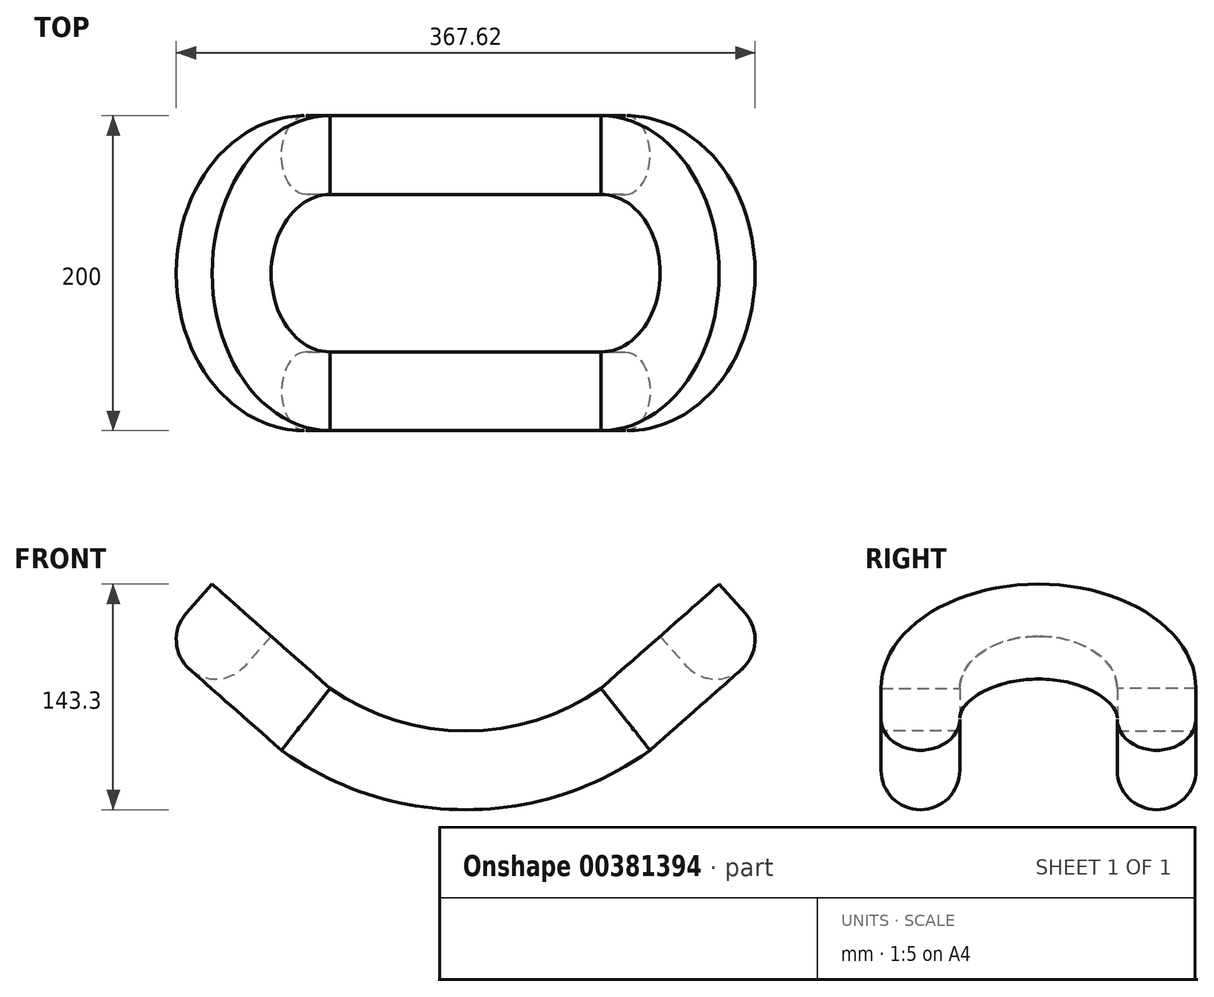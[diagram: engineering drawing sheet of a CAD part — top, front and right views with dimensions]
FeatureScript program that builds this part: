
annotation { "Feature Type Name" : "Feature", "Feature Type Description" : "" }
export const myFeature = defineFeature(function(context is Context, id is Id, definition is map)
    precondition{}
    {
        {
            var Q0;
            Q0=qCreatedBy(makeId("Front.planeOp"),FACE);
            var sketch = newSketch(context, id + "F0", { "sketchPlane" : qUnion([Q0])});
            skArc(sketch, "E0", {"start": v(0, 0) * mm, "mid": v(45.1, 6.94) * mm, "end": v(86.04, 27.13) * mm});
            skLineSegment(sketch, "E1", {"start": v(0, 150) * mm, "end": v(86.04, 27.13) * mm, "construction": true});
            skLineSegment(sketch, "E2", {"start": v(86.04, 27.13) * mm, "end": v(161.01, 93.3) * mm});
            skSolve(sketch);
        }
        {
            var Q0;
            Q0=sQuery(id+"F0.wireOp",EDGE,"E0");
            var Q1;
            Q1=sQuery(id+"F0.wireOp",EDGE,"E2");
            extrude(context, id + "F1", {"bodyType" : ExtendedToolBodyType.SURFACE, "surfaceEntities" : qUnion([Q0, Q1]), "depth" : 100 * mm});
        }
        {
            var Q0;
            Q0=makeQuery(id+"F1.opExtrude","SWEPT_FACE",FACE,{"disambiguationData":[OSD([sQuery(id+"F0.wireOp",EDGE,"E2")])]});
            var sketch = newSketch(context, id + "F2", { "sketchPlane" : qUnion([Q0])});
            skArc(sketch, "E3", {"start": v(82.46, 100) * mm, "mid": v(153.17, 70.71) * mm, "end": v(182.46, 0) * mm});
            skSolve(sketch);
        }
        {
            var Q0;
            Q0=qCreatedBy(makeId("Right.planeOp"),FACE);
            var sketch = newSketch(context, id + "F3", { "sketchPlane" : qUnion([Q0])});
            skLineSegment(sketch, "E4.bottom", {"start": v(-100, 0) * mm, "end": v(-50, 0) * mm});
            skLineSegment(sketch, "E4.left", {"start": v(-100, 0) * mm, "end": v(-100, -25) * mm});
            skLineSegment(sketch, "E4.right", {"start": v(-50, 0) * mm, "end": v(-50, -25) * mm});
            skArc(sketch, "E5", {"start": v(-100, -25) * mm, "mid": v(-75, -50) * mm, "end": v(-50, -25) * mm});
            skSolve(sketch);
        }
        {
            var Q0;
            Q0=makeQuery(id+"F3.imprint","IMPRINT",FACE,{"disambiguationData":[TD([[makeQuery(id+"F3.imprint","IMPRINT",EDGE,{"derivedFrom":sQuery(id+"F3.wireOp",EDGE,"E4.bottom")}),-1.0]])]});
            var Q1;
            Q1=makeQuery(id+"F1.opExtrude","CAP_EDGE",EDGE,{"disambiguationData":[OSD([sQuery(id+"F0.wireOp",EDGE,"E0")])],"isStart":false});
            var Q2;
            Q2=sQuery(id+"F2.wireOp",EDGE,"E3");
            sweep(context, id + "F4", {"profiles" : qUnion([Q0]), "path" : qUnion([Q1, Q2])});
        }
        {
            var Q0;
            Q0=makeQuery(id+"F4.opSweep","SWEPT_BODY",BODY,{"disambiguationData":[OSD([sQuery(id+"F2.wireOp",EDGE,"E3"),sQuery(id+"F3.wireOp",EDGE,"E4.bottom"),sQuery(id+"F3.wireOp",EDGE,"E4.left"),sQuery(id+"F3.wireOp",EDGE,"E4.right"),sQuery(id+"F3.wireOp",EDGE,"E5")])]});
            var Q1;
            Q1=qCreatedBy(makeId("Front.planeOp"),FACE);
            mirror(context, id + "F5", {"operationType" : NewBodyOperationType.ADD, "entities" : qUnion([Q0]), "mirrorPlane" : qUnion([Q1])});
        }
        {
            var Q0;
            Q0=makeQuery(id+"F4.opSweep","SWEPT_BODY",BODY,{"disambiguationData":[OSD([sQuery(id+"F2.wireOp",EDGE,"E3"),sQuery(id+"F3.wireOp",EDGE,"E4.bottom"),sQuery(id+"F3.wireOp",EDGE,"E4.left"),sQuery(id+"F3.wireOp",EDGE,"E4.right"),sQuery(id+"F3.wireOp",EDGE,"E5")])]});
            var Q1;
            Q1=qCreatedBy(makeId("Right.planeOp"),FACE);
            mirror(context, id + "F6", {"operationType" : NewBodyOperationType.ADD, "entities" : qUnion([Q0]), "mirrorPlane" : qUnion([Q1])});
        }
    });
